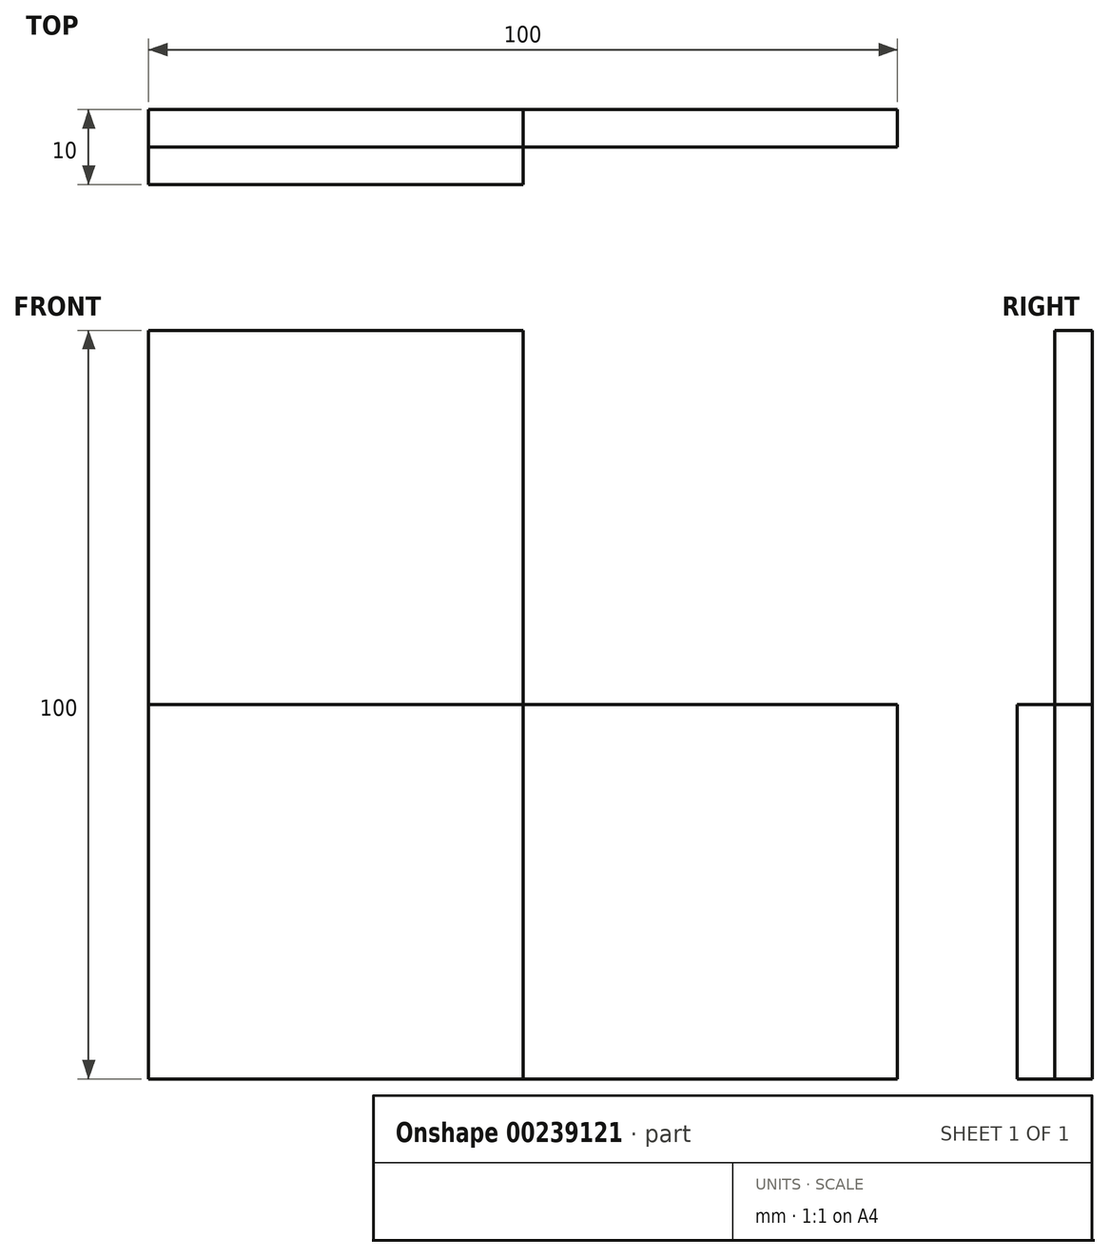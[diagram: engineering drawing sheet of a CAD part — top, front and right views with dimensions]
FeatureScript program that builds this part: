
annotation { "Feature Type Name" : "Feature", "Feature Type Description" : "" }
export const myFeature = defineFeature(function(context is Context, id is Id, definition is map)
    precondition{}
    {
        {
            assignVariable(context, id + "F0", {"name" : "v", "anyValue" : 5});
        }
        {
            var Q0;
            Q0=qCreatedBy(makeId("Front.planeOp"),FACE);
            var sketch = newSketch(context, id + "F1", { "sketchPlane" : qUnion([Q0])});
            skLineSegment(sketch, "E0.bottom", {"start": v(50, 50) * mm, "end": v(-50, 50) * mm});
            skLineSegment(sketch, "E0.top", {"start": v(50, -50) * mm, "end": v(-50, -50) * mm});
            skLineSegment(sketch, "E0.left", {"start": v(50, 50) * mm, "end": v(50, -50) * mm});
            skLineSegment(sketch, "E0.right", {"start": v(-50, 50) * mm, "end": v(-50, -50) * mm});
            skPoint(sketch, "E0.middle", {"position": v(0, 0) * mm});
            skSolve(sketch);
        }
        {
            var Q0;
            Q0 = qSketchRegion(id + "F1", true);
            extrude(context, id + "F2", {"entities" : qUnion([Q0]), "endBound" : BoundingType.SYMMETRIC, "depth" : (2 * getVariable(context, 'v')) * mm});
        }
        {
            var Q0;
            Q0=makeQuery(id+"F2.opExtrude","CAP_FACE",FACE,{"disambiguationData":[OSD([sQuery(id+"F1.wireOp",EDGE,"E0.bottom"),sQuery(id+"F1.wireOp",EDGE,"E0.top"),sQuery(id+"F1.wireOp",EDGE,"E0.left"),sQuery(id+"F1.wireOp",EDGE,"E0.right")])],"isStart":false});
            var sketch = newSketch(context, id + "F3", { "sketchPlane" : qUnion([Q0])});
            skLineSegment(sketch, "E1.bottom", {"start": v(-50, 50) * mm, "end": v(0, 50) * mm});
            skLineSegment(sketch, "E1.top", {"start": v(-50, 0) * mm, "end": v(0, 0) * mm});
            skLineSegment(sketch, "E1.left", {"start": v(-50, 50) * mm, "end": v(-50, 0) * mm});
            skLineSegment(sketch, "E1.right", {"start": v(0, 50) * mm, "end": v(0, 0) * mm});
            skSolve(sketch);
        }
        {
            var Q0;
            Q0 = qSketchRegion(id + "F3", true);
            extrude(context, id + "F4", {"entities" : qUnion([Q0]), "operationType" : NewBodyOperationType.REMOVE, "oppositeDirection" : true, "depth" : (getVariable(context, 'v')) * mm});
        }
        {
            var Q0;
            Q0=makeQuery(id+"F2.opExtrude","CAP_FACE",FACE,{"disambiguationData":[OSD([sQuery(id+"F1.wireOp",EDGE,"E0.bottom"),sQuery(id+"F1.wireOp",EDGE,"E0.top"),sQuery(id+"F1.wireOp",EDGE,"E0.left"),sQuery(id+"F1.wireOp",EDGE,"E0.right")])],"isStart":false});
            var sketch = newSketch(context, id + "F5", { "sketchPlane" : qUnion([Q0])});
            skLineSegment(sketch, "E2.bottom", {"start": v(0, 0) * mm, "end": v(50, 0) * mm});
            skLineSegment(sketch, "E2.top", {"start": v(0, 50) * mm, "end": v(50, 50) * mm});
            skLineSegment(sketch, "E2.left", {"start": v(0, 0) * mm, "end": v(0, 50) * mm});
            skLineSegment(sketch, "E2.right", {"start": v(50, 0) * mm, "end": v(50, 50) * mm});
            skSolve(sketch);
        }
        {
            var Q0;
            Q0 = qSketchRegion(id + "F5", true);
            extrude(context, id + "F6", {"entities" : qUnion([Q0]), "operationType" : NewBodyOperationType.REMOVE, "endBound" : BoundingType.THROUGH_ALL, "oppositeDirection" : true, "depth" : 25 * mm});
        }
        {
            var Q0;
            Q0=makeQuery(id+"F2.opExtrude","CAP_FACE",FACE,{"disambiguationData":[OSD([sQuery(id+"F1.wireOp",EDGE,"E0.bottom"),sQuery(id+"F1.wireOp",EDGE,"E0.top"),sQuery(id+"F1.wireOp",EDGE,"E0.left"),sQuery(id+"F1.wireOp",EDGE,"E0.right")])],"isStart":false});
            var sketch = newSketch(context, id + "F7", { "sketchPlane" : qUnion([Q0])});
            skLineSegment(sketch, "E3.bottom", {"start": v(0, 0) * mm, "end": v(50, 0) * mm});
            skLineSegment(sketch, "E3.top", {"start": v(0, -50) * mm, "end": v(50, -50) * mm});
            skLineSegment(sketch, "E3.left", {"start": v(0, 0) * mm, "end": v(0, -50) * mm});
            skLineSegment(sketch, "E3.right", {"start": v(50, 0) * mm, "end": v(50, -50) * mm});
            skSolve(sketch);
        }
        {
            var Q0;
            Q0 = qSketchRegion(id + "F7", true);
            extrude(context, id + "F8", {"entities" : qUnion([Q0]), "operationType" : NewBodyOperationType.REMOVE, "oppositeDirection" : true, "depth" : (getVariable(context, 'v')) * mm});
        }
    });
